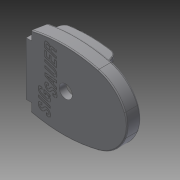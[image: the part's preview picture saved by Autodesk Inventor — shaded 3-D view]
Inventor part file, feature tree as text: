
AUTODESK INVENTOR PART (.ipt)
format: ipt  version: 2014 SP1 (Build 180222100, 222)  size: 4,191,744 bytes
history: native  units: in
note: dims shown in document units (in); Inventor stores cm internally (conversion verified against a paired STEP export)
features: extrude x7, fillet x7, sketch x7, projected_geometry x5, mirror x2, other x1
ambient origin geometry x8: Origin, YZ Plane, XZ Plane, XY Plane, X Axis, Y Axis, Z Axis, Center Point
bodies: Solid1 (feature_tree)
feature tree (29):
  extrude  "Extrusion1"  Depth=1.7367in
  extrude  "Extrusion2"  Depth=0.535in
  fillet  "Fillet1"  Radius=0.864in
  extrude  "Extrusion3"  Depth=0.638in
  mirror  "Mirror1"
  extrude  "Extrusion4"  Depth=0.072in
  extrude  "Extrusion5"  Depth=0.888in
  fillet  "Fillet2"  Radius=0.231in
  mirror  "Mirror2"
  fillet  "Fillet3"  Radius=0.2965in
  fillet  "Fillet4"  Radius=0.118in
  fillet  "Fillet5"  Radius=0.2188in
  fillet  "Fillet6"  [1 undecoded]
  fillet  "Fillet7"  Radius=0.118in
  extrude  "Extrusion6"  Depth=0.3195in
  extrude  "Extrusion7"  Depth=0.118in TaperAngle=0.0deg
  sketch  "Sketch1"  dims[d1=0.2125in d4=1.7367in]
  other  "Image1"
  sketch  "Sketch2"  dims[d25=1.279in d38=0.535in d40=0.864in]
  projected_geometry  "Projected Loop1"
  sketch  "Sketch3"  dims[d41=2.26in d42=0.638in]
  sketch  "Sketch4"  dims[d43=0.5in d44=0.072in]
  sketch  "Sketch5"  dims[d45=0.145in d48=0.888in d49=0.231in d50=0.0in d51=0.2965in d52=0.118in d53=0.0in d54=0.2188in d56=75.0deg d57=0.118in d58=0.0in]
  projected_geometry  "Projected Loop2"
  sketch  "Sketch6"  dims[d59=75.0deg d61=0.3195in]
  sketch  "Sketch7"  dims[d62=0.945in d63=0.118in d64=0.0in d65=0.0875in d66=0.118in d67=0.0in d68=0.1094in d69=0.0312in d70=0.0156in d71=0.0156in d72=0.0156in d73=0.0156in d74=1.118in d75=0.9825in d76=0.0375in d77=0.0in d78=0.3761in d79=0.7382in d80=0.01in d81=0.0in]
  projected_geometry  "Project Cut Edges1"
  projected_geometry  "Project Cut Edges2"
  projected_geometry  "Project Cut Edges3"
note: 1 required parameter value undecoded (feature->parameter linkage not recoverable at this tier; creation-order binding heuristic only, values carry confidence <= 0.55)
